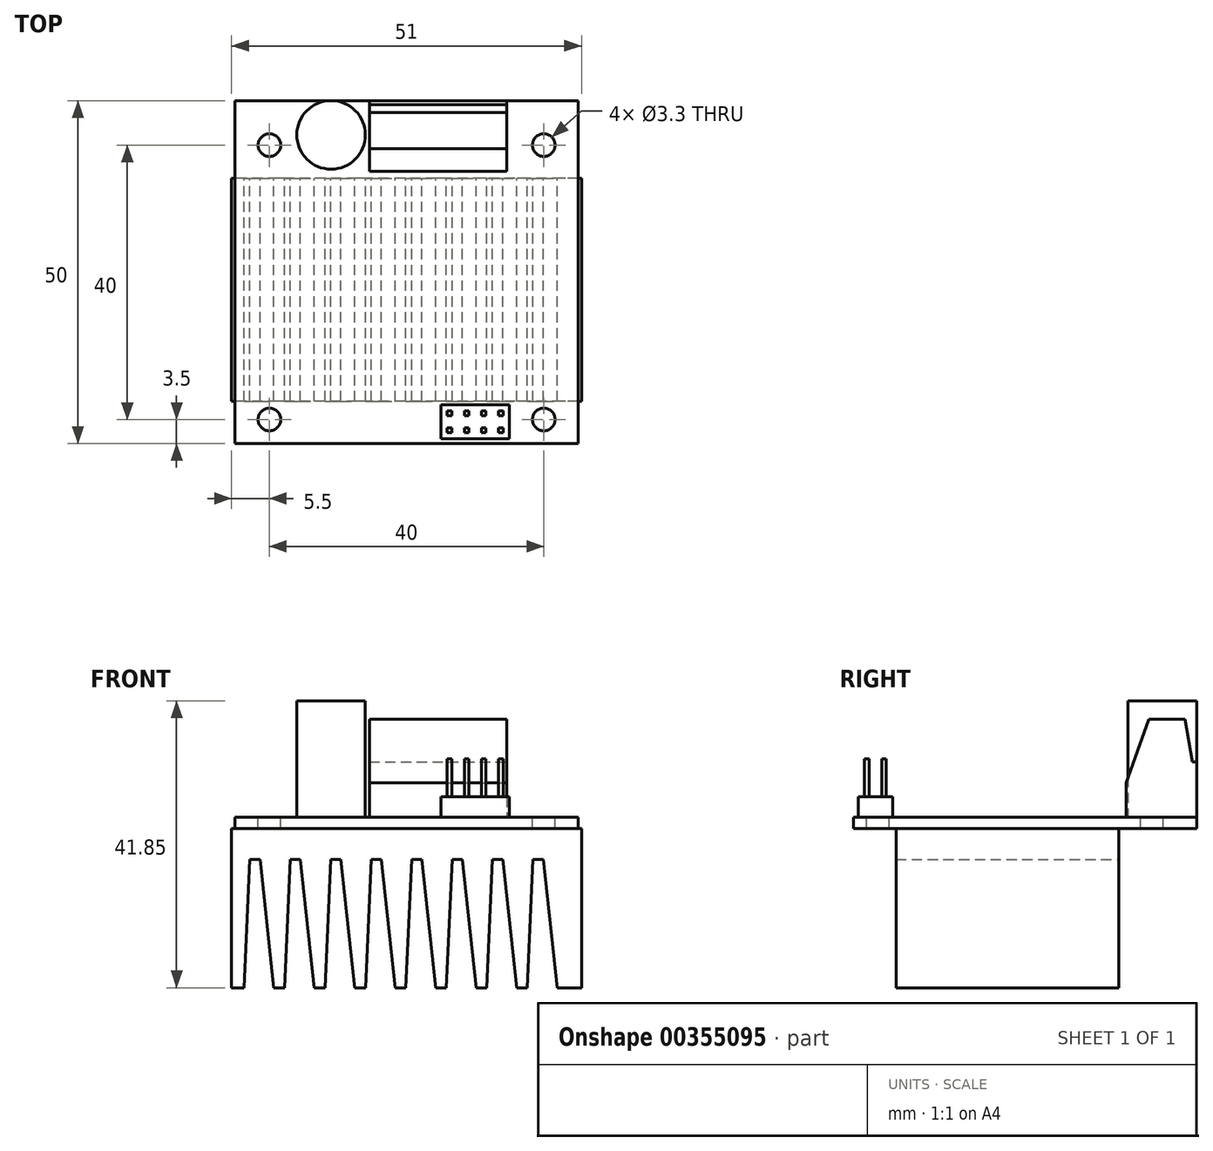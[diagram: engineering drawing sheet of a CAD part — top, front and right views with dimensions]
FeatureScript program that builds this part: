
annotation { "Feature Type Name" : "Feature", "Feature Type Description" : "" }
export const myFeature = defineFeature(function(context is Context, id is Id, definition is map)
    precondition{}
    {
        {
            var Q0;
            Q0=qCreatedBy(makeId("Top.planeOp"),FACE);
            var sketch = newSketch(context, id + "F0", { "sketchPlane" : qUnion([Q0])});
            skLineSegment(sketch, "E0.bottom", {"start": v(25, -25) * mm, "end": v(-25, -25) * mm});
            skLineSegment(sketch, "E0.top", {"start": v(25, 25) * mm, "end": v(-25, 25) * mm});
            skLineSegment(sketch, "E0.left", {"start": v(25, -25) * mm, "end": v(25, 25) * mm});
            skLineSegment(sketch, "E0.right", {"start": v(-25, -25) * mm, "end": v(-25, 25) * mm});
            skPoint(sketch, "E0.middle", {"position": v(0, 0) * mm});
            skSolve(sketch);
        }
        {
            var Q0;
            Q0 = qSketchRegion(id + "F0", true);
            extrude(context, id + "F1", {"entities" : qUnion([Q0]), "depth" : 1.62 * mm});
        }
        {
            var Q0;
            Q0=makeQuery(id+"F1.opExtrude","CAP_FACE",FACE,{"disambiguationData":[OSD([sQuery(id+"F0.wireOp",EDGE,"E0.bottom"),sQuery(id+"F0.wireOp",EDGE,"E0.top"),sQuery(id+"F0.wireOp",EDGE,"E0.left"),sQuery(id+"F0.wireOp",EDGE,"E0.right")])],"isStart":false});
            var sketch = newSketch(context, id + "F2", { "sketchPlane" : qUnion([Q0])});
            skLineSegment(sketch, "E1.bottom", {"start": v(25, -25) * mm, "end": v(-25, -25) * mm});
            skLineSegment(sketch, "E1.top", {"start": v(25, 25) * mm, "end": v(-25, 25) * mm});
            skLineSegment(sketch, "E1.left", {"start": v(25, -25) * mm, "end": v(25, 25) * mm});
            skLineSegment(sketch, "E1.right", {"start": v(-25, -25) * mm, "end": v(-25, 25) * mm});
            skPoint(sketch, "E1.middle", {"position": v(0, 0) * mm});
            skLineSegment(sketch, "E2.bottom", {"start": v(20, -21.5) * mm, "end": v(-20, -21.5) * mm, "construction": true});
            skLineSegment(sketch, "E2.top", {"start": v(20, 18.5) * mm, "end": v(-20, 18.5) * mm, "construction": true});
            skLineSegment(sketch, "E2.left", {"start": v(20, -21.5) * mm, "end": v(20, 18.5) * mm, "construction": true});
            skLineSegment(sketch, "E2.right", {"start": v(-20, -21.5) * mm, "end": v(-20, 18.5) * mm, "construction": true});
            skLineSegment(sketch, "E3.bottom", {"start": v(7.5, -24.33) * mm, "end": v(5, -24.33) * mm});
            skLineSegment(sketch, "E3.top", {"start": v(7.5, -19.33) * mm, "end": v(5, -19.33) * mm});
            skLineSegment(sketch, "E3.left", {"start": v(7.5, -24.33) * mm, "end": v(7.5, -19.33) * mm});
            skLineSegment(sketch, "E3.right", {"start": v(5, -24.33) * mm, "end": v(5, -19.33) * mm});
            skPoint(sketch, "E3.middle", {"position": v(6.25, -21.83) * mm});
            skLineSegment(sketch, "E4.bottom", {"start": v(6.59, -20.92) * mm, "end": v(5.92, -20.92) * mm});
            skLineSegment(sketch, "E4.top", {"start": v(6.59, -20.25) * mm, "end": v(5.92, -20.25) * mm});
            skLineSegment(sketch, "E4.left", {"start": v(6.59, -20.92) * mm, "end": v(6.59, -20.25) * mm});
            skLineSegment(sketch, "E4.right", {"start": v(5.92, -20.92) * mm, "end": v(5.92, -20.25) * mm});
            skPoint(sketch, "E4.middle", {"position": v(6.25, -20.58) * mm});
            skLineSegment(sketch, "E5.bottom", {"start": v(6.59, -23.42) * mm, "end": v(5.92, -23.42) * mm});
            skLineSegment(sketch, "E5.top", {"start": v(6.59, -22.75) * mm, "end": v(5.92, -22.75) * mm});
            skLineSegment(sketch, "E5.left", {"start": v(6.59, -23.42) * mm, "end": v(6.59, -22.75) * mm});
            skLineSegment(sketch, "E5.right", {"start": v(5.92, -23.42) * mm, "end": v(5.92, -22.75) * mm});
            skPoint(sketch, "E5.middle", {"position": v(6.25, -23.08) * mm});
            skLineSegment(sketch, "E6", {"start": v(6.25, -23.08) * mm, "end": v(6.25, -21.83) * mm, "construction": true});
            skLineSegment(sketch, "E7", {"start": v(6.25, -20.58) * mm, "end": v(6.25, -21.83) * mm, "construction": true});
            skLineSegment(sketch, "E8", {"start": v(6.25, -20.58) * mm, "end": v(6.25, -19.33) * mm, "construction": true});
            skLineSegment(sketch, "E9.1.0.0", {"start": v(9.09, -20.92) * mm, "end": v(9.09, -20.24) * mm});
            skPoint(sketch, "E9.1.0.1", {"position": v(8.75, -23.08) * mm});
            skPoint(sketch, "E9.1.0.2", {"position": v(8.75, -20.58) * mm});
            skPoint(sketch, "E9.1.0.3", {"position": v(8.75, -21.83) * mm});
            skLineSegment(sketch, "E9.1.0.4", {"start": v(10, -24.33) * mm, "end": v(7.5, -24.33) * mm});
            skLineSegment(sketch, "E9.1.0.5", {"start": v(10, -19.33) * mm, "end": v(7.5, -19.33) * mm});
            skLineSegment(sketch, "E9.1.0.6", {"start": v(10, -24.33) * mm, "end": v(10, -19.33) * mm});
            skLineSegment(sketch, "E9.1.0.8", {"start": v(8.75, -20.58) * mm, "end": v(8.75, -19.33) * mm, "construction": true});
            skLineSegment(sketch, "E9.1.0.9", {"start": v(8.75, -23.08) * mm, "end": v(8.75, -21.83) * mm, "construction": true});
            skLineSegment(sketch, "E9.1.0.10", {"start": v(9.09, -23.42) * mm, "end": v(9.09, -22.75) * mm});
            skLineSegment(sketch, "E9.1.0.11", {"start": v(9.09, -23.42) * mm, "end": v(8.42, -23.42) * mm});
            skLineSegment(sketch, "E9.1.0.12", {"start": v(8.42, -20.92) * mm, "end": v(8.42, -20.24) * mm});
            skLineSegment(sketch, "E9.1.0.13", {"start": v(9.09, -22.75) * mm, "end": v(8.42, -22.75) * mm});
            skLineSegment(sketch, "E9.1.0.14", {"start": v(9.09, -20.25) * mm, "end": v(8.42, -20.25) * mm});
            skLineSegment(sketch, "E9.1.0.15", {"start": v(8.42, -23.42) * mm, "end": v(8.42, -22.75) * mm});
            skLineSegment(sketch, "E9.1.0.16", {"start": v(8.75, -20.58) * mm, "end": v(8.75, -21.83) * mm, "construction": true});
            skLineSegment(sketch, "E9.1.0.17", {"start": v(9.09, -20.92) * mm, "end": v(8.42, -20.92) * mm});
            skLineSegment(sketch, "E9.2.0.0", {"start": v(11.58, -20.92) * mm, "end": v(11.58, -20.24) * mm});
            skPoint(sketch, "E9.2.0.1", {"position": v(11.25, -23.08) * mm});
            skPoint(sketch, "E9.2.0.2", {"position": v(11.25, -20.58) * mm});
            skPoint(sketch, "E9.2.0.3", {"position": v(11.25, -21.83) * mm});
            skLineSegment(sketch, "E9.2.0.4", {"start": v(12.5, -24.33) * mm, "end": v(10, -24.33) * mm});
            skLineSegment(sketch, "E9.2.0.5", {"start": v(12.5, -19.33) * mm, "end": v(10, -19.33) * mm});
            skLineSegment(sketch, "E9.2.0.6", {"start": v(12.5, -24.33) * mm, "end": v(12.5, -19.33) * mm});
            skLineSegment(sketch, "E9.2.0.7", {"start": v(10, -24.33) * mm, "end": v(10, -19.33) * mm});
            skLineSegment(sketch, "E9.2.0.8", {"start": v(11.25, -20.58) * mm, "end": v(11.25, -19.33) * mm, "construction": true});
            skLineSegment(sketch, "E9.2.0.9", {"start": v(11.25, -23.08) * mm, "end": v(11.25, -21.83) * mm, "construction": true});
            skLineSegment(sketch, "E9.2.0.10", {"start": v(11.58, -23.42) * mm, "end": v(11.58, -22.75) * mm});
            skLineSegment(sketch, "E9.2.0.11", {"start": v(11.58, -23.42) * mm, "end": v(10.91, -23.42) * mm});
            skLineSegment(sketch, "E9.2.0.12", {"start": v(10.91, -20.92) * mm, "end": v(10.91, -20.24) * mm});
            skLineSegment(sketch, "E9.2.0.13", {"start": v(11.58, -22.75) * mm, "end": v(10.91, -22.75) * mm});
            skLineSegment(sketch, "E9.2.0.14", {"start": v(11.58, -20.25) * mm, "end": v(10.91, -20.25) * mm});
            skLineSegment(sketch, "E9.2.0.15", {"start": v(10.91, -23.42) * mm, "end": v(10.91, -22.75) * mm});
            skLineSegment(sketch, "E9.2.0.16", {"start": v(11.25, -20.58) * mm, "end": v(11.25, -21.83) * mm, "construction": true});
            skLineSegment(sketch, "E9.2.0.17", {"start": v(11.58, -20.92) * mm, "end": v(10.91, -20.92) * mm});
            skLineSegment(sketch, "E9.3.0.0", {"start": v(14.08, -20.92) * mm, "end": v(14.08, -20.24) * mm});
            skPoint(sketch, "E9.3.0.1", {"position": v(13.75, -23.08) * mm});
            skPoint(sketch, "E9.3.0.2", {"position": v(13.75, -20.58) * mm});
            skPoint(sketch, "E9.3.0.3", {"position": v(13.75, -21.83) * mm});
            skLineSegment(sketch, "E9.3.0.4", {"start": v(15, -24.33) * mm, "end": v(12.5, -24.33) * mm});
            skLineSegment(sketch, "E9.3.0.5", {"start": v(15, -19.33) * mm, "end": v(12.5, -19.33) * mm});
            skLineSegment(sketch, "E9.3.0.6", {"start": v(15, -24.33) * mm, "end": v(15, -19.33) * mm});
            skLineSegment(sketch, "E9.3.0.7", {"start": v(12.5, -24.33) * mm, "end": v(12.5, -19.33) * mm});
            skLineSegment(sketch, "E9.3.0.8", {"start": v(13.75, -20.58) * mm, "end": v(13.75, -19.33) * mm, "construction": true});
            skLineSegment(sketch, "E9.3.0.9", {"start": v(13.75, -23.08) * mm, "end": v(13.75, -21.83) * mm, "construction": true});
            skLineSegment(sketch, "E9.3.0.10", {"start": v(14.08, -23.42) * mm, "end": v(14.08, -22.75) * mm});
            skLineSegment(sketch, "E9.3.0.11", {"start": v(14.08, -23.42) * mm, "end": v(13.41, -23.42) * mm});
            skLineSegment(sketch, "E9.3.0.12", {"start": v(13.41, -20.92) * mm, "end": v(13.41, -20.24) * mm});
            skLineSegment(sketch, "E9.3.0.13", {"start": v(14.08, -22.75) * mm, "end": v(13.41, -22.75) * mm});
            skLineSegment(sketch, "E9.3.0.14", {"start": v(14.08, -20.25) * mm, "end": v(13.41, -20.25) * mm});
            skLineSegment(sketch, "E9.3.0.15", {"start": v(13.41, -23.42) * mm, "end": v(13.41, -22.75) * mm});
            skLineSegment(sketch, "E9.3.0.16", {"start": v(13.75, -20.58) * mm, "end": v(13.75, -21.83) * mm, "construction": true});
            skLineSegment(sketch, "E9.3.0.17", {"start": v(14.08, -20.92) * mm, "end": v(13.41, -20.92) * mm});
            skLineSegment(sketch, "E9.direction1", {"start": v(5, -24.33) * mm, "end": v(7.5, -24.33) * mm, "construction": true});
            skCircle(sketch, "E10", {"center": v(-11, 20) * mm, "radius": 5 * mm});
            skLineSegment(sketch, "E11.bottom", {"start": v(14.58, 14.7) * mm, "end": v(-5.42, 14.7) * mm});
            skLineSegment(sketch, "E11.top", {"start": v(14.58, 25) * mm, "end": v(-5.42, 25) * mm});
            skLineSegment(sketch, "E11.left", {"start": v(14.58, 14.7) * mm, "end": v(14.58, 25) * mm});
            skLineSegment(sketch, "E11.right", {"start": v(-5.42, 14.7) * mm, "end": v(-5.42, 25) * mm});
            skPoint(sketch, "E11.middle", {"position": v(4.58, 19.85) * mm});
            skSolve(sketch);
        }
        {
            var Q0;
            Q0=makeQuery(id+"F2.imprint","IMPRINT",FACE,{"disambiguationData":[TD([[makeQuery(id+"F2.imprint","IMPRINT",EDGE,{"derivedFrom":sQuery(id+"F2.wireOp",EDGE,"E10")}),1.0]])]});
            extrude(context, id + "F3", {"entities" : qUnion([Q0]), "operationType" : NewBodyOperationType.ADD, "depth" : 17 * mm});
        }
        {
            var Q0;
            Q0=makeQuery(id+"F2.imprint","IMPRINT",FACE,{"disambiguationData":[TD([[makeQuery(id+"F2.imprint","IMPRINT",EDGE,{"derivedFrom":sQuery(id+"F2.wireOp",EDGE,"E11.bottom")}),-1.0]])]});
            extrude(context, id + "F4", {"entities" : qUnion([Q0]), "operationType" : NewBodyOperationType.ADD, "depth" : 14.3 * mm});
        }
        {
            var Q0;
            Q0=makeQuery(id+"F2.imprint","IMPRINT",FACE,{"disambiguationData":[TD([[makeQuery(id+"F2.imprint","IMPRINT",EDGE,{"derivedFrom":sQuery(id+"F2.wireOp",EDGE,"E9.3.0.0")}),-1.0]])]});
            var Q1;
            Q1=makeQuery(id+"F2.imprint","IMPRINT",FACE,{"disambiguationData":[TD([[makeQuery(id+"F2.imprint","IMPRINT",EDGE,{"derivedFrom":sQuery(id+"F2.wireOp",EDGE,"E9.2.0.0")}),-1.0]])]});
            var Q2;
            Q2=makeQuery(id+"F2.imprint","IMPRINT",FACE,{"disambiguationData":[TD([[makeQuery(id+"F2.imprint","IMPRINT",EDGE,{"derivedFrom":sQuery(id+"F2.wireOp",EDGE,"E9.1.0.0")}),-1.0]])]});
            var Q3;
            Q3=makeQuery(id+"F2.imprint","IMPRINT",FACE,{"disambiguationData":[TD([[makeQuery(id+"F2.imprint","IMPRINT",EDGE,{"derivedFrom":sQuery(id+"F2.wireOp",EDGE,"E3.bottom")}),-1.0]])]});
            extrude(context, id + "F5", {"entities" : qUnion([Q0, Q1, Q2, Q3]), "operationType" : NewBodyOperationType.ADD, "depth" : 3 * mm});
        }
        {
            var Q0;
            Q0=makeQuery(id+"F2.imprint","IMPRINT",FACE,{"disambiguationData":[TD([[makeQuery(id+"F2.imprint","IMPRINT",EDGE,{"derivedFrom":sQuery(id+"F2.wireOp",EDGE,"E4.bottom")}),-1.0]])]});
            var Q1;
            Q1=makeQuery(id+"F2.imprint","IMPRINT",FACE,{"disambiguationData":[TD([[makeQuery(id+"F2.imprint","IMPRINT",EDGE,{"derivedFrom":sQuery(id+"F2.wireOp",EDGE,"E5.bottom")}),-1.0]])]});
            var Q2;
            Q2=makeQuery(id+"F2.imprint","IMPRINT",FACE,{"disambiguationData":[TD([[makeQuery(id+"F2.imprint","IMPRINT",EDGE,{"derivedFrom":sQuery(id+"F2.wireOp",EDGE,"E9.1.0.10")}),1.0]])]});
            var Q3;
            Q3=makeQuery(id+"F2.imprint","IMPRINT",FACE,{"disambiguationData":[TD([[makeQuery(id+"F2.imprint","IMPRINT",EDGE,{"derivedFrom":sQuery(id+"F2.wireOp",EDGE,"E9.1.0.0")}),1.0]])]});
            var Q4;
            Q4=makeQuery(id+"F2.imprint","IMPRINT",FACE,{"disambiguationData":[TD([[makeQuery(id+"F2.imprint","IMPRINT",EDGE,{"derivedFrom":sQuery(id+"F2.wireOp",EDGE,"E9.2.0.0")}),1.0]])]});
            var Q5;
            Q5=makeQuery(id+"F2.imprint","IMPRINT",FACE,{"disambiguationData":[TD([[makeQuery(id+"F2.imprint","IMPRINT",EDGE,{"derivedFrom":sQuery(id+"F2.wireOp",EDGE,"E9.2.0.10")}),1.0]])]});
            var Q6;
            Q6=makeQuery(id+"F2.imprint","IMPRINT",FACE,{"disambiguationData":[TD([[makeQuery(id+"F2.imprint","IMPRINT",EDGE,{"derivedFrom":sQuery(id+"F2.wireOp",EDGE,"E9.3.0.10")}),1.0]])]});
            var Q7;
            Q7=makeQuery(id+"F2.imprint","IMPRINT",FACE,{"disambiguationData":[TD([[makeQuery(id+"F2.imprint","IMPRINT",EDGE,{"derivedFrom":sQuery(id+"F2.wireOp",EDGE,"E9.3.0.0")}),1.0]])]});
            extrude(context, id + "F6", {"entities" : qUnion([Q0, Q1, Q2, Q3, Q4, Q5, Q6, Q7]), "operationType" : NewBodyOperationType.ADD, "depth" : 8.5 * mm});
        }
        {
            var Q0;
            Q0=sQuery(id+"F2.wireOp",VERTEX,"E2.top.end");
            var Q1;
            Q1=sQuery(id+"F2.wireOp",VERTEX,"E2.bottom.end");
            var Q2;
            Q2=sQuery(id+"F2.wireOp",VERTEX,"E2.left.start");
            var Q3;
            Q3=sQuery(id+"F2.wireOp",VERTEX,"E2.top.start");
            var Q4;
            Q4=makeQuery(id+"F1.opExtrude","SWEPT_BODY",BODY,{"disambiguationData":[OSD([sQuery(id+"F0.wireOp",EDGE,"E0.bottom"),sQuery(id+"F0.wireOp",EDGE,"E0.top"),sQuery(id+"F0.wireOp",EDGE,"E0.left"),sQuery(id+"F0.wireOp",EDGE,"E0.right")])]});
            hole(context, id + "F7", {"style" : HoleStyle.SIMPLE, "endStyle" : HoleEndStyle.THROUGH, "holeDiameter" : 3.3 * mm, "tappedDepth" : 12 * mm, "tapClearance" : 3, "locations" : qUnion([Q0, Q1, Q2, Q3]), "scope" : qUnion([Q4])});
        }
        {
            var Q0;
            Q0=qCreatedBy(makeId("Front.planeOp"),FACE);
            var sketch = newSketch(context, id + "F8", { "sketchPlane" : qUnion([Q0])});
            skLineSegment(sketch, "E12.bottom", {"start": v(25.5, 0) * mm, "end": v(-25.5, 0) * mm});
            skLineSegment(sketch, "E12.top", {"start": v(25.5, -23.23) * mm, "end": v(21.96, -23.23) * mm});
            skLineSegment(sketch, "E12.left", {"start": v(25.5, 0) * mm, "end": v(25.5, -23.23) * mm});
            skLineSegment(sketch, "E12.right", {"start": v(-25.5, 0) * mm, "end": v(-25.5, -23.23) * mm});
            skPoint(sketch, "E12.middle", {"position": v(0, -11.62) * mm});
            skLineSegment(sketch, "E13", {"start": v(-23.7, -23.23) * mm, "end": v(-22.86, -4.5) * mm});
            skLineSegment(sketch, "E14", {"start": v(-22.86, -4.5) * mm, "end": v(-21.37, -4.5) * mm});
            skLineSegment(sketch, "E15", {"start": v(-21.37, -4.5) * mm, "end": v(-19.34, -23.23) * mm});
            skLineSegment(sketch, "E16.1.0.0", {"start": v(-15.47, -4.5) * mm, "end": v(-13.44, -23.23) * mm});
            skLineSegment(sketch, "E16.1.0.1", {"start": v(-17.8, -23.23) * mm, "end": v(-16.96, -4.5) * mm});
            skLineSegment(sketch, "E16.1.0.2", {"start": v(-16.96, -4.5) * mm, "end": v(-15.47, -4.5) * mm});
            skLineSegment(sketch, "E16.2.0.0", {"start": v(-9.57, -4.5) * mm, "end": v(-7.54, -23.23) * mm});
            skLineSegment(sketch, "E16.2.0.1", {"start": v(-11.9, -23.23) * mm, "end": v(-11.06, -4.5) * mm});
            skLineSegment(sketch, "E16.2.0.2", {"start": v(-11.06, -4.5) * mm, "end": v(-9.57, -4.5) * mm});
            skLineSegment(sketch, "E16.3.0.0", {"start": v(-3.67, -4.5) * mm, "end": v(-1.64, -23.23) * mm});
            skLineSegment(sketch, "E16.3.0.1", {"start": v(-6, -23.23) * mm, "end": v(-5.16, -4.5) * mm});
            skLineSegment(sketch, "E16.3.0.2", {"start": v(-5.16, -4.5) * mm, "end": v(-3.67, -4.5) * mm});
            skLineSegment(sketch, "E16.4.0.0", {"start": v(2.23, -4.5) * mm, "end": v(4.26, -23.23) * mm});
            skLineSegment(sketch, "E16.4.0.1", {"start": v(-0.1, -23.23) * mm, "end": v(0.74, -4.5) * mm});
            skLineSegment(sketch, "E16.4.0.2", {"start": v(0.74, -4.5) * mm, "end": v(2.23, -4.5) * mm});
            skLineSegment(sketch, "E16.5.0.0", {"start": v(8.13, -4.5) * mm, "end": v(10.16, -23.23) * mm});
            skLineSegment(sketch, "E16.5.0.1", {"start": v(5.8, -23.23) * mm, "end": v(6.64, -4.5) * mm});
            skLineSegment(sketch, "E16.5.0.2", {"start": v(6.64, -4.5) * mm, "end": v(8.13, -4.5) * mm});
            skLineSegment(sketch, "E16.6.0.0", {"start": v(14.03, -4.5) * mm, "end": v(16.06, -23.23) * mm});
            skLineSegment(sketch, "E16.6.0.1", {"start": v(11.7, -23.23) * mm, "end": v(12.54, -4.5) * mm});
            skLineSegment(sketch, "E16.6.0.2", {"start": v(12.54, -4.5) * mm, "end": v(14.03, -4.5) * mm});
            skLineSegment(sketch, "E16.7.0.0", {"start": v(19.93, -4.5) * mm, "end": v(21.96, -23.23) * mm});
            skLineSegment(sketch, "E16.7.0.1", {"start": v(17.6, -23.23) * mm, "end": v(18.44, -4.5) * mm});
            skLineSegment(sketch, "E16.7.0.2", {"start": v(18.44, -4.5) * mm, "end": v(19.93, -4.5) * mm});
            skLineSegment(sketch, "E16.direction1", {"start": v(-19.34, -23.23) * mm, "end": v(-17.8, -23.23) * mm, "construction": true});
            skLineSegment(sketch, "E17.trimOffspring", {"start": v(-17.8, -23.23) * mm, "end": v(-19.34, -23.23) * mm});
            skLineSegment(sketch, "E18.trimOffspring", {"start": v(-23.7, -23.23) * mm, "end": v(-25.5, -23.23) * mm});
            skLineSegment(sketch, "E19.trimOffspring", {"start": v(-11.9, -23.23) * mm, "end": v(-13.44, -23.23) * mm});
            skLineSegment(sketch, "E20.trimOffspring", {"start": v(-6, -23.23) * mm, "end": v(-7.54, -23.23) * mm});
            skLineSegment(sketch, "E21.trimOffspring", {"start": v(-0.1, -23.23) * mm, "end": v(-1.64, -23.23) * mm});
            skLineSegment(sketch, "E22.trimOffspring", {"start": v(5.8, -23.23) * mm, "end": v(4.26, -23.23) * mm});
            skLineSegment(sketch, "E23.trimOffspring", {"start": v(11.7, -23.23) * mm, "end": v(10.16, -23.23) * mm});
            skLineSegment(sketch, "E24.trimOffspring", {"start": v(17.6, -23.23) * mm, "end": v(16.06, -23.23) * mm});
            skSolve(sketch);
        }
        {
            var Q0;
            Q0 = qSketchRegion(id + "F8", true);
            extrude(context, id + "F9", {"entities" : qUnion([Q0]), "operationType" : NewBodyOperationType.ADD, "depth" : (25 - 6.16) * mm, "hasSecondDirection" : true, "secondDirectionOppositeDirection" : true, "secondDirectionDepth" : (25 - 11.34) * mm});
        }
        {
            var Q0;
            Q0=makeQuery(id+"F4.opExtrude","SWEPT_FACE",FACE,{"disambiguationData":[OSD([sQuery(id+"F2.wireOp",EDGE,"E11.left")])]});
            var sketch = newSketch(context, id + "F10", { "sketchPlane" : qUnion([Q0])});
            skLineSegment(sketch, "E25", {"start": v(14.7, 6.68) * mm, "end": v(18, 15.92) * mm});
            skLineSegment(sketch, "E26", {"start": v(23.28, 15.92) * mm, "end": v(24.4, 9.7) * mm});
            skLineSegment(sketch, "E27", {"start": v(24.4, 9.7) * mm, "end": v(25, 9.7) * mm});
            skSolve(sketch);
        }
        {
            var Q0;
            Q0 = qSketchRegion(id + "F10", true);
            var Q1;
            {var subQ0=sQuery(id+"F10.wireOp",EDGE,"E25");Q1=makeQuery(id+"F10.imprint","IMPRINT",FACE,{"disambiguationData":[TD([[makeQuery(id+"F10.imprint","IMPRINT",EDGE,{"derivedFrom":subQ0}),1.0]])]});}
            var Q2;
            {var subQ0=sQuery(id+"F10.wireOp",EDGE,"E26");Q2=makeQuery(id+"F10.imprint","IMPRINT",FACE,{"disambiguationData":[TD([[makeQuery(id+"F10.imprint","IMPRINT",EDGE,{"derivedFrom":subQ0}),1.0]])]});}
            extrude(context, id + "F11", {"entities" : qUnion([Q0, Q1, Q2]), "operationType" : NewBodyOperationType.REMOVE, "oppositeDirection" : true, "depth" : 20 * mm});
        }
    });
